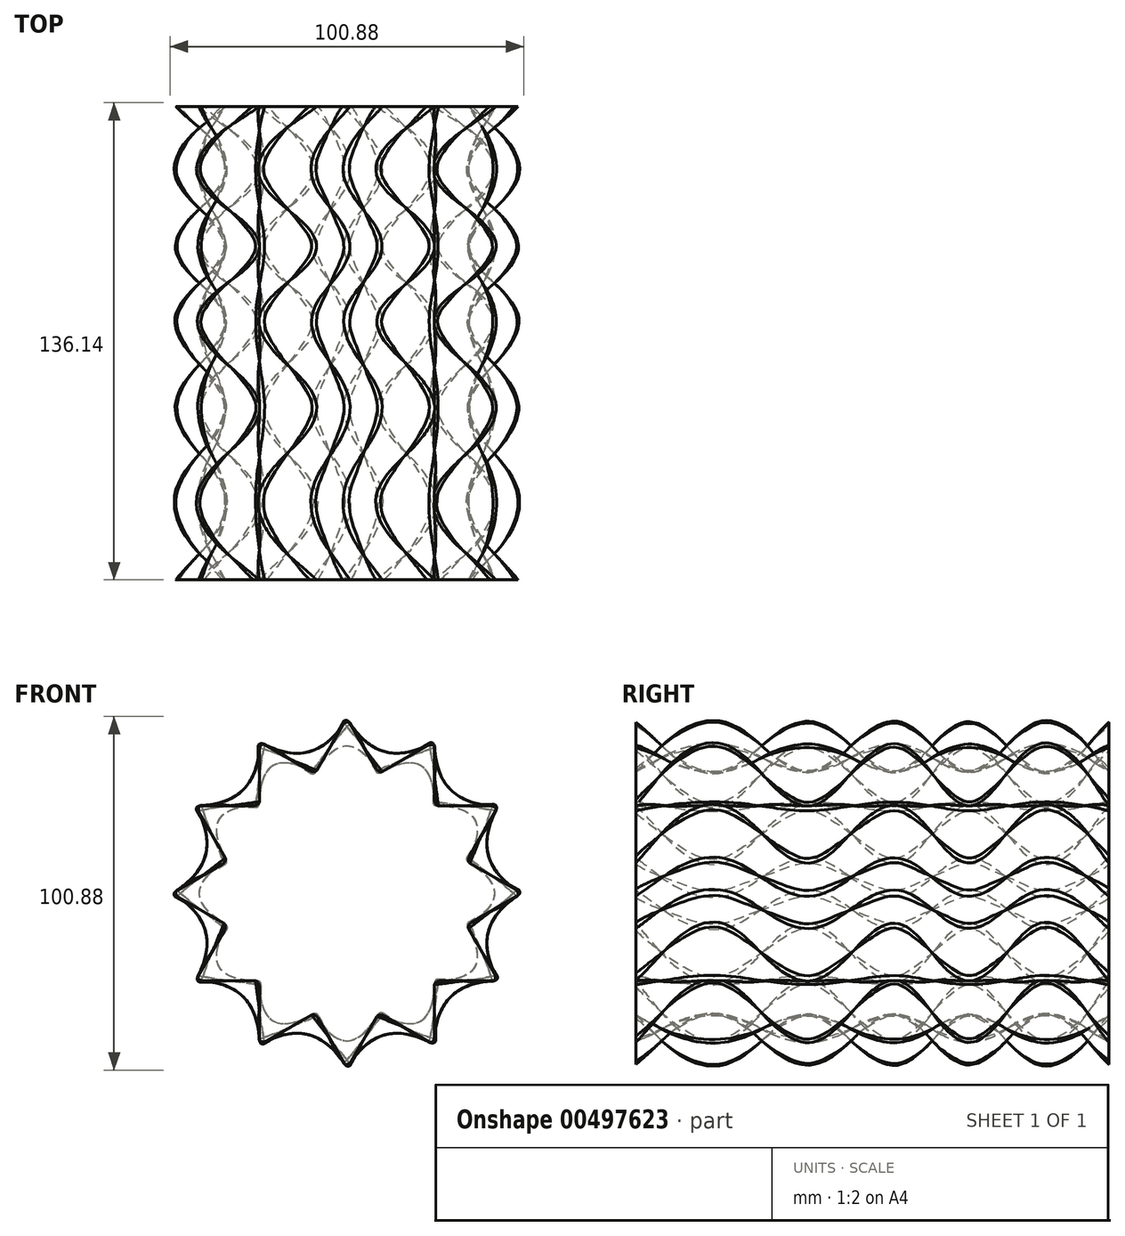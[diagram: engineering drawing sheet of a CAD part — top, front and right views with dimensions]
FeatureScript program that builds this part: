
annotation { "Feature Type Name" : "Feature", "Feature Type Description" : "" }
export const myFeature = defineFeature(function(context is Context, id is Id, definition is map)
    precondition{}
    {
        {
            var Q0;
            Q0=qCreatedBy(makeId("Front.planeOp"),FACE);
            cPlane(context, id + "F0", {"entities" : qUnion([Q0]), "cplaneType" : CPlaneType.OFFSET, "offset" : 20 * mm, "width" : 150 * mm, "height" : 150 * mm});
        }
        {
            var Q0;
            Q0=qCreatedBy(id+"F0.planeOp",FACE);
            cPlane(context, id + "F1", {"entities" : qUnion([Q0]), "cplaneType" : CPlaneType.OFFSET, "offset" : 20 * mm, "width" : 150 * mm, "height" : 150 * mm});
        }
        {
            var Q0;
            Q0=qCreatedBy(id+"F0.planeOp",FACE);
            cPlane(context, id + "F2", {"entities" : qUnion([Q0]), "cplaneType" : CPlaneType.OFFSET, "offset" : 40 * mm, "width" : 150 * mm, "height" : 150 * mm});
        }
        {
            var Q0;
            Q0=qCreatedBy(id+"F2.planeOp",FACE);
            cPlane(context, id + "F3", {"entities" : qUnion([Q0]), "cplaneType" : CPlaneType.OFFSET, "offset" : 25 * mm, "width" : 150 * mm, "height" : 150 * mm});
        }
        {
            var Q0;
            Q0=qCreatedBy(id+"F3.planeOp",FACE);
            cPlane(context, id + "F4", {"entities" : qUnion([Q0]), "cplaneType" : CPlaneType.OFFSET, "offset" : 25 * mm, "width" : 150 * mm, "height" : 150 * mm});
        }
        {
            var Q0;
            Q0=qCreatedBy(id+"F4.planeOp",FACE);
            cPlane(context, id + "F5", {"entities" : qUnion([Q0]), "cplaneType" : CPlaneType.OFFSET, "offset" : 25 * mm, "width" : 150 * mm, "height" : 150 * mm});
        }
        {
            var Q0;
            Q0=qCreatedBy(makeId("Front.planeOp"),FACE);
            var sketch = newSketch(context, id + "F6", { "sketchPlane" : qUnion([Q0])});
            skCircle(sketch, "E0", {"center": v(0, 0) * mm, "radius": 50 * mm});
            skCircle(sketch, "E1.cCircle", {"center": v(0, 0) * mm, "radius": 50 * mm, "construction": true});
            skLineSegment(sketch, "E1.0", {"start": v(50, 0) * mm, "end": v(34.15, -9.15) * mm});
            skLineSegment(sketch, "E1.1", {"start": v(-25, -43.3) * mm, "end": v(-25, -25) * mm});
            skLineSegment(sketch, "E1.2", {"start": v(-25, 43.3) * mm, "end": v(-9.15, 34.15) * mm});
            skPoint(sketch, "E2", {"position": v(12.5, 21.65) * mm});
            skLineSegment(sketch, "E3.0", {"start": v(0, 50) * mm, "end": v(9.15, 34.15) * mm});
            skLineSegment(sketch, "E3.1", {"start": v(43.3, -25) * mm, "end": v(25, -25) * mm});
            skLineSegment(sketch, "E3.2", {"start": v(-43.3, -25) * mm, "end": v(-34.15, -9.15) * mm});
            skLineSegment(sketch, "E4.0", {"start": v(25, 43.3) * mm, "end": v(25, 25) * mm});
            skLineSegment(sketch, "E4.1", {"start": v(25, -43.3) * mm, "end": v(9.15, -34.15) * mm});
            skLineSegment(sketch, "E4.2", {"start": v(-50, 0) * mm, "end": v(-34.15, 9.15) * mm});
            skLineSegment(sketch, "E5.0", {"start": v(43.3, 25) * mm, "end": v(34.15, 9.15) * mm});
            skLineSegment(sketch, "E5.1", {"start": v(0, -50) * mm, "end": v(-9.15, -34.15) * mm});
            skLineSegment(sketch, "E5.2", {"start": v(-43.3, 25) * mm, "end": v(-25, 25) * mm});
            skLineSegment(sketch, "E6.trimOffspring", {"start": v(34.15, 9.15) * mm, "end": v(50, 0) * mm});
            skLineSegment(sketch, "E7.trimOffspring", {"start": v(25, -25) * mm, "end": v(25, -43.3) * mm});
            skLineSegment(sketch, "E8.trimOffspring", {"start": v(25, 25) * mm, "end": v(43.3, 25) * mm});
            skLineSegment(sketch, "E9.trimOffspring", {"start": v(9.15, 34.15) * mm, "end": v(25, 43.3) * mm});
            skLineSegment(sketch, "E10.trimOffspring", {"start": v(-9.15, 34.15) * mm, "end": v(0, 50) * mm});
            skLineSegment(sketch, "E11.trimOffspring", {"start": v(-25, 25) * mm, "end": v(-25, 43.3) * mm});
            skLineSegment(sketch, "E12.trimOffspring", {"start": v(-34.15, 9.15) * mm, "end": v(-43.3, 25) * mm});
            skLineSegment(sketch, "E13.trimOffspring", {"start": v(-34.15, -9.15) * mm, "end": v(-50, 0) * mm});
            skLineSegment(sketch, "E14.trimOffspring", {"start": v(-25, -25) * mm, "end": v(-43.3, -25) * mm});
            skLineSegment(sketch, "E15.trimOffspring", {"start": v(-9.15, -34.15) * mm, "end": v(-25, -43.3) * mm});
            skLineSegment(sketch, "E16.trimOffspring", {"start": v(9.15, -34.15) * mm, "end": v(0, -50) * mm});
            skLineSegment(sketch, "E17.trimOffspring", {"start": v(34.15, -9.15) * mm, "end": v(43.3, -25) * mm});
            skSolve(sketch);
        }
        {
            var Q0;
            Q0=qCreatedBy(id+"F0.planeOp",FACE);
            var sketch = newSketch(context, id + "F7", { "sketchPlane" : qUnion([Q0])});
            skLineSegment(sketch, "E18", {"start": v(0, 50) * mm, "end": v(9.15, 34.15) * mm});
            skLineSegment(sketch, "E19", {"start": v(9.15, 34.15) * mm, "end": v(25, 43.3) * mm});
            skLineSegment(sketch, "E20.1.0", {"start": v(-25, 43.3) * mm, "end": v(-9.15, 34.15) * mm});
            skLineSegment(sketch, "E20.1.1", {"start": v(-9.15, 34.15) * mm, "end": v(0, 50) * mm});
            skLineSegment(sketch, "E20.2.0", {"start": v(-43.3, 25) * mm, "end": v(-25, 25) * mm});
            skLineSegment(sketch, "E20.2.1", {"start": v(-25, 25) * mm, "end": v(-25, 43.3) * mm});
            skLineSegment(sketch, "E20.3.0", {"start": v(-50, 0) * mm, "end": v(-34.15, 9.15) * mm});
            skLineSegment(sketch, "E20.3.1", {"start": v(-34.15, 9.15) * mm, "end": v(-43.3, 25) * mm});
            skLineSegment(sketch, "E20.4.0", {"start": v(-43.3, -25) * mm, "end": v(-34.15, -9.15) * mm});
            skLineSegment(sketch, "E20.4.1", {"start": v(-34.15, -9.15) * mm, "end": v(-50, 0) * mm});
            skLineSegment(sketch, "E20.5.0", {"start": v(-25, -43.3) * mm, "end": v(-25, -25) * mm});
            skLineSegment(sketch, "E20.5.1", {"start": v(-25, -25) * mm, "end": v(-43.3, -25) * mm});
            skLineSegment(sketch, "E20.6.0", {"start": v(0, -50) * mm, "end": v(-9.15, -34.15) * mm});
            skLineSegment(sketch, "E20.6.1", {"start": v(-9.15, -34.15) * mm, "end": v(-25, -43.3) * mm});
            skLineSegment(sketch, "E20.7.0", {"start": v(25, -43.3) * mm, "end": v(9.15, -34.15) * mm});
            skLineSegment(sketch, "E20.7.1", {"start": v(9.15, -34.15) * mm, "end": v(0, -50) * mm});
            skLineSegment(sketch, "E20.8.0", {"start": v(43.3, -25) * mm, "end": v(25, -25) * mm});
            skLineSegment(sketch, "E20.8.1", {"start": v(25, -25) * mm, "end": v(25, -43.3) * mm});
            skLineSegment(sketch, "E20.9.0", {"start": v(50, 0) * mm, "end": v(34.15, -9.15) * mm});
            skLineSegment(sketch, "E20.9.1", {"start": v(34.15, -9.15) * mm, "end": v(43.3, -25) * mm});
            skLineSegment(sketch, "E20.10.0", {"start": v(43.3, 25) * mm, "end": v(34.15, 9.15) * mm});
            skLineSegment(sketch, "E20.10.1", {"start": v(34.15, 9.15) * mm, "end": v(50, 0) * mm});
            skLineSegment(sketch, "E20.11.0", {"start": v(25, 43.3) * mm, "end": v(25, 25) * mm});
            skLineSegment(sketch, "E20.11.1", {"start": v(25, 25) * mm, "end": v(43.3, 25) * mm});
            skPoint(sketch, "E20.center", {"position": v(0, 0) * mm});
            skSolve(sketch);
        }
        {
            var Q0;
            Q0=qCreatedBy(id+"F2.planeOp",FACE);
            var sketch = newSketch(context, id + "F8", { "sketchPlane" : qUnion([Q0])});
            skPoint(sketch, "E21.center", {"position": v(0, 0) * mm});
            skLineSegment(sketch, "E22", {"start": v(-9.15, 34.15) * mm, "end": v(0, 50) * mm});
            skLineSegment(sketch, "E23", {"start": v(0, 50) * mm, "end": v(9.15, 34.15) * mm});
            skLineSegment(sketch, "E24.1.2", {"start": v(-25, 43.3) * mm, "end": v(-9.15, 34.15) * mm});
            skLineSegment(sketch, "E24.1.3", {"start": v(-25, 25) * mm, "end": v(-25, 43.3) * mm});
            skLineSegment(sketch, "E24.2.2", {"start": v(-43.3, 25) * mm, "end": v(-25, 25) * mm});
            skLineSegment(sketch, "E24.2.3", {"start": v(-34.15, 9.15) * mm, "end": v(-43.3, 25) * mm});
            skLineSegment(sketch, "E24.3.2", {"start": v(-50, 0) * mm, "end": v(-34.15, 9.15) * mm});
            skLineSegment(sketch, "E24.3.3", {"start": v(-34.15, -9.15) * mm, "end": v(-50, 0) * mm});
            skLineSegment(sketch, "E24.4.2", {"start": v(-43.3, -25) * mm, "end": v(-34.15, -9.15) * mm});
            skLineSegment(sketch, "E24.4.3", {"start": v(-25, -25) * mm, "end": v(-43.3, -25) * mm});
            skLineSegment(sketch, "E24.5.2", {"start": v(-25, -43.3) * mm, "end": v(-25, -25) * mm});
            skLineSegment(sketch, "E24.5.3", {"start": v(-9.15, -34.15) * mm, "end": v(-25, -43.3) * mm});
            skLineSegment(sketch, "E24.6.2", {"start": v(0, -50) * mm, "end": v(-9.15, -34.15) * mm});
            skLineSegment(sketch, "E24.6.3", {"start": v(9.15, -34.15) * mm, "end": v(0, -50) * mm});
            skLineSegment(sketch, "E24.7.2", {"start": v(25, -43.3) * mm, "end": v(9.15, -34.15) * mm});
            skLineSegment(sketch, "E24.7.3", {"start": v(25, -25) * mm, "end": v(25, -43.3) * mm});
            skLineSegment(sketch, "E24.8.2", {"start": v(43.3, -25) * mm, "end": v(25, -25) * mm});
            skLineSegment(sketch, "E24.8.3", {"start": v(34.15, -9.15) * mm, "end": v(43.3, -25) * mm});
            skLineSegment(sketch, "E24.9.2", {"start": v(50, 0) * mm, "end": v(34.15, -9.15) * mm});
            skLineSegment(sketch, "E24.9.3", {"start": v(34.15, 9.15) * mm, "end": v(50, 0) * mm});
            skLineSegment(sketch, "E24.10.2", {"start": v(43.3, 25) * mm, "end": v(34.15, 9.15) * mm});
            skLineSegment(sketch, "E24.10.3", {"start": v(25, 25) * mm, "end": v(43.3, 25) * mm});
            skLineSegment(sketch, "E24.11.2", {"start": v(25, 43.3) * mm, "end": v(25, 25) * mm});
            skLineSegment(sketch, "E24.11.3", {"start": v(9.15, 34.15) * mm, "end": v(25, 43.3) * mm});
            skSolve(sketch);
        }
        {
            var Q0;
            Q0=qCreatedBy(id+"F1.planeOp",FACE);
            var sketch = newSketch(context, id + "F9", { "sketchPlane" : qUnion([Q0])});
            skLineSegment(sketch, "E25", {"start": v(0, 50) * mm, "end": v(-9.15, 34.15) * mm});
            skLineSegment(sketch, "E26", {"start": v(0, 50) * mm, "end": v(9.15, 34.15) * mm});
            skLineSegment(sketch, "E27.1.0", {"start": v(-25, 43.3) * mm, "end": v(-9.15, 34.15) * mm});
            skLineSegment(sketch, "E27.1.1", {"start": v(-25, 43.3) * mm, "end": v(-25, 25) * mm});
            skLineSegment(sketch, "E27.2.0", {"start": v(-43.3, 25) * mm, "end": v(-25, 25) * mm});
            skLineSegment(sketch, "E27.2.1", {"start": v(-43.3, 25) * mm, "end": v(-34.15, 9.15) * mm});
            skLineSegment(sketch, "E27.3.0", {"start": v(-50, 0) * mm, "end": v(-34.15, 9.15) * mm});
            skLineSegment(sketch, "E27.3.1", {"start": v(-50, 0) * mm, "end": v(-34.15, -9.15) * mm});
            skLineSegment(sketch, "E27.4.0", {"start": v(-43.3, -25) * mm, "end": v(-34.15, -9.15) * mm});
            skLineSegment(sketch, "E27.4.1", {"start": v(-43.3, -25) * mm, "end": v(-25, -25) * mm});
            skLineSegment(sketch, "E27.5.0", {"start": v(-25, -43.3) * mm, "end": v(-25, -25) * mm});
            skLineSegment(sketch, "E27.5.1", {"start": v(-25, -43.3) * mm, "end": v(-9.15, -34.15) * mm});
            skLineSegment(sketch, "E27.6.0", {"start": v(0, -50) * mm, "end": v(-9.15, -34.15) * mm});
            skLineSegment(sketch, "E27.6.1", {"start": v(0, -50) * mm, "end": v(9.15, -34.15) * mm});
            skLineSegment(sketch, "E27.7.0", {"start": v(25, -43.3) * mm, "end": v(9.15, -34.15) * mm});
            skLineSegment(sketch, "E27.7.1", {"start": v(25, -43.3) * mm, "end": v(25, -25) * mm});
            skLineSegment(sketch, "E27.8.0", {"start": v(43.3, -25) * mm, "end": v(25, -25) * mm});
            skLineSegment(sketch, "E27.8.1", {"start": v(43.3, -25) * mm, "end": v(34.15, -9.15) * mm});
            skLineSegment(sketch, "E27.9.0", {"start": v(50, 0) * mm, "end": v(34.15, -9.15) * mm});
            skLineSegment(sketch, "E27.9.1", {"start": v(50, 0) * mm, "end": v(34.15, 9.15) * mm});
            skLineSegment(sketch, "E27.10.0", {"start": v(43.3, 25) * mm, "end": v(34.15, 9.15) * mm});
            skLineSegment(sketch, "E27.10.1", {"start": v(43.3, 25) * mm, "end": v(25, 25) * mm});
            skLineSegment(sketch, "E27.11.0", {"start": v(25, 43.3) * mm, "end": v(25, 25) * mm});
            skLineSegment(sketch, "E27.11.1", {"start": v(25, 43.3) * mm, "end": v(9.15, 34.15) * mm});
            skPoint(sketch, "E27.center", {"position": v(0, 0) * mm});
            skSolve(sketch);
        }
        {
            var Q0;
            Q0=qCreatedBy(id+"F3.planeOp",FACE);
            var sketch = newSketch(context, id + "F10", { "sketchPlane" : qUnion([Q0])});
            skCircle(sketch, "E28.cCircle", {"center": v(0, 0) * mm, "radius": 50 * mm, "construction": true});
            skLineSegment(sketch, "E29", {"start": v(0, 50) * mm, "end": v(9.15, 34.15) * mm});
            skLineSegment(sketch, "E30", {"start": v(25, 43.3) * mm, "end": v(9.15, 34.15) * mm});
            skLineSegment(sketch, "E31.1.0", {"start": v(0, 50) * mm, "end": v(-9.15, 34.15) * mm});
            skLineSegment(sketch, "E31.1.1", {"start": v(-25, 43.3) * mm, "end": v(-9.15, 34.15) * mm});
            skLineSegment(sketch, "E31.2.0", {"start": v(-25, 43.3) * mm, "end": v(-25, 25) * mm});
            skLineSegment(sketch, "E31.2.1", {"start": v(-43.3, 25) * mm, "end": v(-25, 25) * mm});
            skLineSegment(sketch, "E31.3.0", {"start": v(-43.3, 25) * mm, "end": v(-34.15, 9.15) * mm});
            skLineSegment(sketch, "E31.3.1", {"start": v(-50, 0) * mm, "end": v(-34.15, 9.15) * mm});
            skLineSegment(sketch, "E31.4.0", {"start": v(-50, 0) * mm, "end": v(-34.15, -9.15) * mm});
            skLineSegment(sketch, "E31.4.1", {"start": v(-43.3, -25) * mm, "end": v(-34.15, -9.15) * mm});
            skLineSegment(sketch, "E31.5.0", {"start": v(-43.3, -25) * mm, "end": v(-25, -25) * mm});
            skLineSegment(sketch, "E31.5.1", {"start": v(-25, -43.3) * mm, "end": v(-25, -25) * mm});
            skLineSegment(sketch, "E31.6.0", {"start": v(-25, -43.3) * mm, "end": v(-9.15, -34.15) * mm});
            skLineSegment(sketch, "E31.6.1", {"start": v(0, -50) * mm, "end": v(-9.15, -34.15) * mm});
            skLineSegment(sketch, "E31.7.0", {"start": v(0, -50) * mm, "end": v(9.15, -34.15) * mm});
            skLineSegment(sketch, "E31.7.1", {"start": v(25, -43.3) * mm, "end": v(9.15, -34.15) * mm});
            skLineSegment(sketch, "E31.8.0", {"start": v(25, -43.3) * mm, "end": v(25, -25) * mm});
            skLineSegment(sketch, "E31.8.1", {"start": v(43.3, -25) * mm, "end": v(25, -25) * mm});
            skLineSegment(sketch, "E31.9.0", {"start": v(43.3, -25) * mm, "end": v(34.15, -9.15) * mm});
            skLineSegment(sketch, "E31.9.1", {"start": v(50, 0) * mm, "end": v(34.15, -9.15) * mm});
            skLineSegment(sketch, "E31.10.0", {"start": v(50, 0) * mm, "end": v(34.15, 9.15) * mm});
            skLineSegment(sketch, "E31.10.1", {"start": v(43.3, 25) * mm, "end": v(34.15, 9.15) * mm});
            skLineSegment(sketch, "E31.11.0", {"start": v(43.3, 25) * mm, "end": v(25, 25) * mm});
            skLineSegment(sketch, "E31.11.1", {"start": v(25, 43.3) * mm, "end": v(25, 25) * mm});
            skSolve(sketch);
        }
        {
            var Q0;
            Q0=qCreatedBy(id+"F4.planeOp",FACE);
            var sketch = newSketch(context, id + "F11", { "sketchPlane" : qUnion([Q0])});
            skLineSegment(sketch, "E32", {"start": v(0, 50) * mm, "end": v(9.15, 34.15) * mm});
            skLineSegment(sketch, "E33", {"start": v(25, 43.3) * mm, "end": v(9.15, 34.15) * mm});
            skLineSegment(sketch, "E34.1.0", {"start": v(0, 50) * mm, "end": v(-9.15, 34.15) * mm});
            skLineSegment(sketch, "E34.1.1", {"start": v(-25, 43.3) * mm, "end": v(-9.15, 34.15) * mm});
            skLineSegment(sketch, "E34.2.0", {"start": v(-25, 43.3) * mm, "end": v(-25, 25) * mm});
            skLineSegment(sketch, "E34.2.1", {"start": v(-43.3, 25) * mm, "end": v(-25, 25) * mm});
            skLineSegment(sketch, "E34.3.0", {"start": v(-43.3, 25) * mm, "end": v(-34.15, 9.15) * mm});
            skLineSegment(sketch, "E34.3.1", {"start": v(-50, 0) * mm, "end": v(-34.15, 9.15) * mm});
            skLineSegment(sketch, "E34.4.0", {"start": v(-50, 0) * mm, "end": v(-34.15, -9.15) * mm});
            skLineSegment(sketch, "E34.4.1", {"start": v(-43.3, -25) * mm, "end": v(-34.15, -9.15) * mm});
            skLineSegment(sketch, "E34.5.0", {"start": v(-43.3, -25) * mm, "end": v(-25, -25) * mm});
            skLineSegment(sketch, "E34.5.1", {"start": v(-25, -43.3) * mm, "end": v(-25, -25) * mm});
            skLineSegment(sketch, "E34.6.0", {"start": v(-25, -43.3) * mm, "end": v(-9.15, -34.15) * mm});
            skLineSegment(sketch, "E34.6.1", {"start": v(0, -50) * mm, "end": v(-9.15, -34.15) * mm});
            skLineSegment(sketch, "E34.7.0", {"start": v(0, -50) * mm, "end": v(9.15, -34.15) * mm});
            skLineSegment(sketch, "E34.7.1", {"start": v(25, -43.3) * mm, "end": v(9.15, -34.15) * mm});
            skLineSegment(sketch, "E34.8.0", {"start": v(25, -43.3) * mm, "end": v(25, -25) * mm});
            skLineSegment(sketch, "E34.8.1", {"start": v(43.3, -25) * mm, "end": v(25, -25) * mm});
            skLineSegment(sketch, "E34.9.0", {"start": v(43.3, -25) * mm, "end": v(34.15, -9.15) * mm});
            skLineSegment(sketch, "E34.9.1", {"start": v(50, 0) * mm, "end": v(34.15, -9.15) * mm});
            skLineSegment(sketch, "E34.10.0", {"start": v(50, 0) * mm, "end": v(34.15, 9.15) * mm});
            skLineSegment(sketch, "E34.10.1", {"start": v(43.3, 25) * mm, "end": v(34.15, 9.15) * mm});
            skLineSegment(sketch, "E34.11.0", {"start": v(43.3, 25) * mm, "end": v(25, 25) * mm});
            skLineSegment(sketch, "E34.11.1", {"start": v(25, 43.3) * mm, "end": v(25, 25) * mm});
            skPoint(sketch, "E34.center", {"position": v(0, 0) * mm});
            skSolve(sketch);
        }
        {
            var Q0;
            Q0=qCreatedBy(id+"F5.planeOp",FACE);
            var sketch = newSketch(context, id + "F12", { "sketchPlane" : qUnion([Q0])});
            skLineSegment(sketch, "E35", {"start": v(0, 50) * mm, "end": v(9.15, 34.15) * mm});
            skLineSegment(sketch, "E36", {"start": v(9.15, 34.15) * mm, "end": v(25, 43.3) * mm});
            skLineSegment(sketch, "E37.1.0", {"start": v(-9.15, 34.15) * mm, "end": v(0, 50) * mm});
            skLineSegment(sketch, "E37.1.1", {"start": v(-25, 43.3) * mm, "end": v(-9.15, 34.15) * mm});
            skLineSegment(sketch, "E37.2.0", {"start": v(-25, 25) * mm, "end": v(-25, 43.3) * mm});
            skLineSegment(sketch, "E37.2.1", {"start": v(-43.3, 25) * mm, "end": v(-25, 25) * mm});
            skLineSegment(sketch, "E37.3.0", {"start": v(-34.15, 9.15) * mm, "end": v(-43.3, 25) * mm});
            skLineSegment(sketch, "E37.3.1", {"start": v(-50, 0) * mm, "end": v(-34.15, 9.15) * mm});
            skLineSegment(sketch, "E37.4.0", {"start": v(-34.15, -9.15) * mm, "end": v(-50, 0) * mm});
            skLineSegment(sketch, "E37.4.1", {"start": v(-43.3, -25) * mm, "end": v(-34.15, -9.15) * mm});
            skLineSegment(sketch, "E37.5.0", {"start": v(-25, -25) * mm, "end": v(-43.3, -25) * mm});
            skLineSegment(sketch, "E37.5.1", {"start": v(-25, -43.3) * mm, "end": v(-25, -25) * mm});
            skLineSegment(sketch, "E37.6.0", {"start": v(-9.15, -34.15) * mm, "end": v(-25, -43.3) * mm});
            skLineSegment(sketch, "E37.6.1", {"start": v(0, -50) * mm, "end": v(-9.15, -34.15) * mm});
            skLineSegment(sketch, "E37.7.0", {"start": v(9.15, -34.15) * mm, "end": v(0, -50) * mm});
            skLineSegment(sketch, "E37.7.1", {"start": v(25, -43.3) * mm, "end": v(9.15, -34.15) * mm});
            skLineSegment(sketch, "E37.8.0", {"start": v(25, -25) * mm, "end": v(25, -43.3) * mm});
            skLineSegment(sketch, "E37.8.1", {"start": v(43.3, -25) * mm, "end": v(25, -25) * mm});
            skLineSegment(sketch, "E37.9.0", {"start": v(34.15, -9.15) * mm, "end": v(43.3, -25) * mm});
            skLineSegment(sketch, "E37.9.1", {"start": v(50, 0) * mm, "end": v(34.15, -9.15) * mm});
            skLineSegment(sketch, "E37.10.0", {"start": v(34.15, 9.15) * mm, "end": v(50, 0) * mm});
            skLineSegment(sketch, "E37.10.1", {"start": v(43.3, 25) * mm, "end": v(34.15, 9.15) * mm});
            skLineSegment(sketch, "E37.11.0", {"start": v(25, 25) * mm, "end": v(43.3, 25) * mm});
            skLineSegment(sketch, "E37.11.1", {"start": v(25, 43.3) * mm, "end": v(25, 25) * mm});
            skPoint(sketch, "E37.center", {"position": v(0, 0) * mm});
            skSolve(sketch);
        }
        {
            var Q0;
            Q0=makeQuery(id+"F6.imprint","IMPRINT",FACE,{"disambiguationData":[TD([[makeQuery(id+"F6.imprint","IMPRINT",EDGE,{"derivedFrom":sQuery(id+"F6.wireOp",EDGE,"E1.0")}),-1.0]])]});
            var Q1;
            Q1=makeQuery(id+"F7.imprint","IMPRINT",FACE,{"disambiguationData":[TD([[makeQuery(id+"F7.imprint","IMPRINT",EDGE,{"derivedFrom":sQuery(id+"F7.wireOp",EDGE,"E18")}),-1.0]])]});
            var Q2;
            Q2=makeQuery(id+"F9.imprint","IMPRINT",FACE,{"disambiguationData":[TD([[makeQuery(id+"F9.imprint","IMPRINT",EDGE,{"derivedFrom":sQuery(id+"F9.wireOp",EDGE,"E25")}),1.0]])]});
            var Q3;
            Q3=makeQuery(id+"F8.imprint","IMPRINT",FACE,{"disambiguationData":[TD([[makeQuery(id+"F8.imprint","IMPRINT",EDGE,{"derivedFrom":sQuery(id+"F8.wireOp",EDGE,"E22")}),-1.0]])]});
            var Q4;
            Q4=makeQuery(id+"F10.imprint","IMPRINT",FACE,{"disambiguationData":[TD([[makeQuery(id+"F10.imprint","IMPRINT",EDGE,{"derivedFrom":sQuery(id+"F10.wireOp",EDGE,"E29")}),-1.0]])]});
            var Q5;
            Q5=makeQuery(id+"F11.imprint","IMPRINT",FACE,{"disambiguationData":[TD([[makeQuery(id+"F11.imprint","IMPRINT",EDGE,{"derivedFrom":sQuery(id+"F11.wireOp",EDGE,"E32")}),-1.0]])]});
            var Q6;
            Q6=makeQuery(id+"F12.imprint","IMPRINT",FACE,{"disambiguationData":[TD([[makeQuery(id+"F12.imprint","IMPRINT",EDGE,{"derivedFrom":sQuery(id+"F12.wireOp",EDGE,"E35")}),-1.0]])]});
            var Q7;
            Q7=sQuery(id+"F6.wireOp",VERTEX,"E4.0.start");
            var Q8;
            Q8=sQuery(id+"F7.wireOp",VERTEX,"E19.start");
            var Q9;
            Q9=sQuery(id+"F9.wireOp",VERTEX,"E27.11.0.start");
            var Q10;
            Q10=sQuery(id+"F8.wireOp",VERTEX,"E23.end");
            var Q11;
            Q11=sQuery(id+"F10.wireOp",VERTEX,"E31.11.1.start");
            var Q12;
            Q12=sQuery(id+"F11.wireOp",VERTEX,"E33.end");
            var Q13;
            Q13=sQuery(id+"F12.wireOp",VERTEX,"E37.11.1.start");
            loft(context, id + "F13", {"sheetProfilesArray" : [{ "sheetProfileEntities" : qUnion([Q0]) }, { "sheetProfileEntities" : qUnion([Q1]) }, { "sheetProfileEntities" : qUnion([Q2]) }, { "sheetProfileEntities" : qUnion([Q3]) }, { "sheetProfileEntities" : qUnion([Q4]) }, { "sheetProfileEntities" : qUnion([Q5]) }, { "sheetProfileEntities" : qUnion([Q6]) }], "matchConnections" : true, "connections" : [{ "connectionEntities" : qUnion([Q7, Q8, Q9, Q10, Q11, Q12, Q13]), "connectionEdgeQueries" : qUnion([]), "connectionEdgeParameters" : [] }]});
        }
        {
            var Q0;
            {var subQ0=sQuery(id+"F6.wireOp",EDGE,"E0");Q0=qUnion([makeQuery(id+"F13.opLoft","SWEPT_EDGE",EDGE,{"disambiguationData":[OSD([subQ0,sQuery(id+"F6.wireOp",EDGE,"E4.1"),sQuery(id+"F6.wireOp",EDGE,"E7.trimOffspring"),sQuery(id+"F7.wireOp",EDGE,"E20.8.0"),sQuery(id+"F7.wireOp",EDGE,"E20.8.1"),sQuery(id+"F8.wireOp",EDGE,"E24.7.3"),sQuery(id+"F8.wireOp",EDGE,"E24.8.2"),sQuery(id+"F9.wireOp",EDGE,"E27.7.0"),sQuery(id+"F9.wireOp",EDGE,"E27.7.1"),sQuery(id+"F10.wireOp",EDGE,"E31.7.1"),sQuery(id+"F10.wireOp",EDGE,"E31.8.0"),sQuery(id+"F11.wireOp",EDGE,"E34.8.0"),sQuery(id+"F11.wireOp",EDGE,"E34.8.1"),sQuery(id+"F12.wireOp",EDGE,"E37.7.1"),sQuery(id+"F12.wireOp",EDGE,"E37.8.0")])]}),makeQuery(id+"F13.opLoft","SWEPT_EDGE",EDGE,{"disambiguationData":[OSD([subQ0,sQuery(id+"F6.wireOp",EDGE,"E5.1"),sQuery(id+"F6.wireOp",EDGE,"E16.trimOffspring"),sQuery(id+"F7.wireOp",EDGE,"E20.7.0"),sQuery(id+"F7.wireOp",EDGE,"E20.7.1"),sQuery(id+"F8.wireOp",EDGE,"E24.6.3"),sQuery(id+"F8.wireOp",EDGE,"E24.7.2"),sQuery(id+"F9.wireOp",EDGE,"E27.6.0"),sQuery(id+"F9.wireOp",EDGE,"E27.6.1"),sQuery(id+"F10.wireOp",EDGE,"E31.6.1"),sQuery(id+"F10.wireOp",EDGE,"E31.7.0"),sQuery(id+"F11.wireOp",EDGE,"E34.7.0"),sQuery(id+"F11.wireOp",EDGE,"E34.7.1"),sQuery(id+"F12.wireOp",EDGE,"E37.6.1"),sQuery(id+"F12.wireOp",EDGE,"E37.7.0")])]})]);}
            var Q1;
            {Q1=qUnion([makeQuery(id+"F13.opLoft","SWEPT_EDGE",EDGE,{"disambiguationData":[OSD([sQuery(id+"F6.wireOp",EDGE,"E3.1"),sQuery(id+"F6.wireOp",EDGE,"E7.trimOffspring"),sQuery(id+"F7.wireOp",EDGE,"E20.8.0"),sQuery(id+"F7.wireOp",EDGE,"E20.9.1"),sQuery(id+"F8.wireOp",EDGE,"E24.8.2"),sQuery(id+"F8.wireOp",EDGE,"E24.8.3"),sQuery(id+"F9.wireOp",EDGE,"E27.7.1"),sQuery(id+"F9.wireOp",EDGE,"E27.8.0"),sQuery(id+"F10.wireOp",EDGE,"E31.8.0"),sQuery(id+"F10.wireOp",EDGE,"E31.8.1"),sQuery(id+"F11.wireOp",EDGE,"E34.8.1"),sQuery(id+"F11.wireOp",EDGE,"E34.9.0"),sQuery(id+"F12.wireOp",EDGE,"E37.8.0"),sQuery(id+"F12.wireOp",EDGE,"E37.8.1")])]}),makeQuery(id+"F13.opLoft","SWEPT_EDGE",EDGE,{"disambiguationData":[OSD([sQuery(id+"F6.wireOp",EDGE,"E4.1"),sQuery(id+"F6.wireOp",EDGE,"E16.trimOffspring"),sQuery(id+"F7.wireOp",EDGE,"E20.7.0"),sQuery(id+"F7.wireOp",EDGE,"E20.8.1"),sQuery(id+"F8.wireOp",EDGE,"E24.7.2"),sQuery(id+"F8.wireOp",EDGE,"E24.7.3"),sQuery(id+"F9.wireOp",EDGE,"E27.6.1"),sQuery(id+"F9.wireOp",EDGE,"E27.7.0"),sQuery(id+"F10.wireOp",EDGE,"E31.7.0"),sQuery(id+"F10.wireOp",EDGE,"E31.7.1"),sQuery(id+"F11.wireOp",EDGE,"E34.7.1"),sQuery(id+"F11.wireOp",EDGE,"E34.8.0"),sQuery(id+"F12.wireOp",EDGE,"E37.7.0"),sQuery(id+"F12.wireOp",EDGE,"E37.7.1")])]})]);}
            var Q2;
            {Q2=qUnion([makeQuery(id+"F13.opLoft","SWEPT_EDGE",EDGE,{"disambiguationData":[OSD([sQuery(id+"F6.wireOp",EDGE,"E4.1"),sQuery(id+"F6.wireOp",EDGE,"E16.trimOffspring"),sQuery(id+"F7.wireOp",EDGE,"E20.7.0"),sQuery(id+"F7.wireOp",EDGE,"E20.8.1"),sQuery(id+"F8.wireOp",EDGE,"E24.7.2"),sQuery(id+"F8.wireOp",EDGE,"E24.7.3"),sQuery(id+"F9.wireOp",EDGE,"E27.6.1"),sQuery(id+"F9.wireOp",EDGE,"E27.7.0"),sQuery(id+"F10.wireOp",EDGE,"E31.7.0"),sQuery(id+"F10.wireOp",EDGE,"E31.7.1"),sQuery(id+"F11.wireOp",EDGE,"E34.7.1"),sQuery(id+"F11.wireOp",EDGE,"E34.8.0"),sQuery(id+"F12.wireOp",EDGE,"E37.7.0"),sQuery(id+"F12.wireOp",EDGE,"E37.7.1")])]}),makeQuery(id+"F13.opLoft","SWEPT_EDGE",EDGE,{"disambiguationData":[OSD([sQuery(id+"F6.wireOp",EDGE,"E5.1"),sQuery(id+"F6.wireOp",EDGE,"E15.trimOffspring"),sQuery(id+"F7.wireOp",EDGE,"E20.6.0"),sQuery(id+"F7.wireOp",EDGE,"E20.7.1"),sQuery(id+"F8.wireOp",EDGE,"E24.6.2"),sQuery(id+"F8.wireOp",EDGE,"E24.6.3"),sQuery(id+"F9.wireOp",EDGE,"E27.5.1"),sQuery(id+"F9.wireOp",EDGE,"E27.6.0"),sQuery(id+"F10.wireOp",EDGE,"E31.6.0"),sQuery(id+"F10.wireOp",EDGE,"E31.6.1"),sQuery(id+"F11.wireOp",EDGE,"E34.6.1"),sQuery(id+"F11.wireOp",EDGE,"E34.7.0"),sQuery(id+"F12.wireOp",EDGE,"E37.6.0"),sQuery(id+"F12.wireOp",EDGE,"E37.6.1")])]})]);}
            var Q3;
            {var subQ0=sQuery(id+"F6.wireOp",EDGE,"E0");Q3=qUnion([makeQuery(id+"F13.opLoft","SWEPT_EDGE",EDGE,{"disambiguationData":[OSD([subQ0,sQuery(id+"F6.wireOp",EDGE,"E1.1"),sQuery(id+"F6.wireOp",EDGE,"E15.trimOffspring"),sQuery(id+"F7.wireOp",EDGE,"E20.6.0"),sQuery(id+"F7.wireOp",EDGE,"E20.6.1"),sQuery(id+"F8.wireOp",EDGE,"E24.5.3"),sQuery(id+"F8.wireOp",EDGE,"E24.6.2"),sQuery(id+"F9.wireOp",EDGE,"E27.5.0"),sQuery(id+"F9.wireOp",EDGE,"E27.5.1"),sQuery(id+"F10.wireOp",EDGE,"E31.5.1"),sQuery(id+"F10.wireOp",EDGE,"E31.6.0"),sQuery(id+"F11.wireOp",EDGE,"E34.6.0"),sQuery(id+"F11.wireOp",EDGE,"E34.6.1"),sQuery(id+"F12.wireOp",EDGE,"E37.5.1"),sQuery(id+"F12.wireOp",EDGE,"E37.6.0")])]}),makeQuery(id+"F13.opLoft","SWEPT_EDGE",EDGE,{"disambiguationData":[OSD([subQ0,sQuery(id+"F6.wireOp",EDGE,"E5.1"),sQuery(id+"F6.wireOp",EDGE,"E16.trimOffspring"),sQuery(id+"F7.wireOp",EDGE,"E20.7.0"),sQuery(id+"F7.wireOp",EDGE,"E20.7.1"),sQuery(id+"F8.wireOp",EDGE,"E24.6.3"),sQuery(id+"F8.wireOp",EDGE,"E24.7.2"),sQuery(id+"F9.wireOp",EDGE,"E27.6.0"),sQuery(id+"F9.wireOp",EDGE,"E27.6.1"),sQuery(id+"F10.wireOp",EDGE,"E31.6.1"),sQuery(id+"F10.wireOp",EDGE,"E31.7.0"),sQuery(id+"F11.wireOp",EDGE,"E34.7.0"),sQuery(id+"F11.wireOp",EDGE,"E34.7.1"),sQuery(id+"F12.wireOp",EDGE,"E37.6.1"),sQuery(id+"F12.wireOp",EDGE,"E37.7.0")])]})]);}
            var Q4;
            {Q4=qUnion([makeQuery(id+"F13.opLoft","SWEPT_EDGE",EDGE,{"disambiguationData":[OSD([sQuery(id+"F6.wireOp",EDGE,"E1.1"),sQuery(id+"F6.wireOp",EDGE,"E14.trimOffspring"),sQuery(id+"F7.wireOp",EDGE,"E20.5.0"),sQuery(id+"F7.wireOp",EDGE,"E20.6.1"),sQuery(id+"F8.wireOp",EDGE,"E24.5.2"),sQuery(id+"F8.wireOp",EDGE,"E24.5.3"),sQuery(id+"F9.wireOp",EDGE,"E27.4.1"),sQuery(id+"F9.wireOp",EDGE,"E27.5.0"),sQuery(id+"F10.wireOp",EDGE,"E31.5.0"),sQuery(id+"F10.wireOp",EDGE,"E31.5.1"),sQuery(id+"F11.wireOp",EDGE,"E34.5.1"),sQuery(id+"F11.wireOp",EDGE,"E34.6.0"),sQuery(id+"F12.wireOp",EDGE,"E37.5.0"),sQuery(id+"F12.wireOp",EDGE,"E37.5.1")])]}),makeQuery(id+"F13.opLoft","SWEPT_EDGE",EDGE,{"disambiguationData":[OSD([sQuery(id+"F6.wireOp",EDGE,"E5.1"),sQuery(id+"F6.wireOp",EDGE,"E15.trimOffspring"),sQuery(id+"F7.wireOp",EDGE,"E20.6.0"),sQuery(id+"F7.wireOp",EDGE,"E20.7.1"),sQuery(id+"F8.wireOp",EDGE,"E24.6.2"),sQuery(id+"F8.wireOp",EDGE,"E24.6.3"),sQuery(id+"F9.wireOp",EDGE,"E27.5.1"),sQuery(id+"F9.wireOp",EDGE,"E27.6.0"),sQuery(id+"F10.wireOp",EDGE,"E31.6.0"),sQuery(id+"F10.wireOp",EDGE,"E31.6.1"),sQuery(id+"F11.wireOp",EDGE,"E34.6.1"),sQuery(id+"F11.wireOp",EDGE,"E34.7.0"),sQuery(id+"F12.wireOp",EDGE,"E37.6.0"),sQuery(id+"F12.wireOp",EDGE,"E37.6.1")])]})]);}
            var Q5;
            {var subQ0=sQuery(id+"F6.wireOp",EDGE,"E0");Q5=qUnion([makeQuery(id+"F13.opLoft","SWEPT_EDGE",EDGE,{"disambiguationData":[OSD([subQ0,sQuery(id+"F6.wireOp",EDGE,"E3.1"),sQuery(id+"F6.wireOp",EDGE,"E17.trimOffspring"),sQuery(id+"F7.wireOp",EDGE,"E20.9.0"),sQuery(id+"F7.wireOp",EDGE,"E20.9.1"),sQuery(id+"F8.wireOp",EDGE,"E24.8.3"),sQuery(id+"F8.wireOp",EDGE,"E24.9.2"),sQuery(id+"F9.wireOp",EDGE,"E27.8.0"),sQuery(id+"F9.wireOp",EDGE,"E27.8.1"),sQuery(id+"F10.wireOp",EDGE,"E31.8.1"),sQuery(id+"F10.wireOp",EDGE,"E31.9.0"),sQuery(id+"F11.wireOp",EDGE,"E34.9.0"),sQuery(id+"F11.wireOp",EDGE,"E34.9.1"),sQuery(id+"F12.wireOp",EDGE,"E37.8.1"),sQuery(id+"F12.wireOp",EDGE,"E37.9.0")])]}),makeQuery(id+"F13.opLoft","SWEPT_EDGE",EDGE,{"disambiguationData":[OSD([subQ0,sQuery(id+"F6.wireOp",EDGE,"E4.1"),sQuery(id+"F6.wireOp",EDGE,"E7.trimOffspring"),sQuery(id+"F7.wireOp",EDGE,"E20.8.0"),sQuery(id+"F7.wireOp",EDGE,"E20.8.1"),sQuery(id+"F8.wireOp",EDGE,"E24.7.3"),sQuery(id+"F8.wireOp",EDGE,"E24.8.2"),sQuery(id+"F9.wireOp",EDGE,"E27.7.0"),sQuery(id+"F9.wireOp",EDGE,"E27.7.1"),sQuery(id+"F10.wireOp",EDGE,"E31.7.1"),sQuery(id+"F10.wireOp",EDGE,"E31.8.0"),sQuery(id+"F11.wireOp",EDGE,"E34.8.0"),sQuery(id+"F11.wireOp",EDGE,"E34.8.1"),sQuery(id+"F12.wireOp",EDGE,"E37.7.1"),sQuery(id+"F12.wireOp",EDGE,"E37.8.0")])]})]);}
            var Q6;
            {var subQ0=sQuery(id+"F6.wireOp",EDGE,"E0");Q6=qUnion([makeQuery(id+"F13.opLoft","SWEPT_EDGE",EDGE,{"disambiguationData":[OSD([subQ0,sQuery(id+"F6.wireOp",EDGE,"E3.1"),sQuery(id+"F6.wireOp",EDGE,"E17.trimOffspring"),sQuery(id+"F7.wireOp",EDGE,"E20.9.0"),sQuery(id+"F7.wireOp",EDGE,"E20.9.1"),sQuery(id+"F8.wireOp",EDGE,"E24.8.3"),sQuery(id+"F8.wireOp",EDGE,"E24.9.2"),sQuery(id+"F9.wireOp",EDGE,"E27.8.0"),sQuery(id+"F9.wireOp",EDGE,"E27.8.1"),sQuery(id+"F10.wireOp",EDGE,"E31.8.1"),sQuery(id+"F10.wireOp",EDGE,"E31.9.0"),sQuery(id+"F11.wireOp",EDGE,"E34.9.0"),sQuery(id+"F11.wireOp",EDGE,"E34.9.1"),sQuery(id+"F12.wireOp",EDGE,"E37.8.1"),sQuery(id+"F12.wireOp",EDGE,"E37.9.0")])]}),makeQuery(id+"F13.opLoft","SWEPT_EDGE",EDGE,{"disambiguationData":[OSD([subQ0,sQuery(id+"F6.wireOp",EDGE,"E4.1"),sQuery(id+"F6.wireOp",EDGE,"E7.trimOffspring"),sQuery(id+"F7.wireOp",EDGE,"E20.8.0"),sQuery(id+"F7.wireOp",EDGE,"E20.8.1"),sQuery(id+"F8.wireOp",EDGE,"E24.7.3"),sQuery(id+"F8.wireOp",EDGE,"E24.8.2"),sQuery(id+"F9.wireOp",EDGE,"E27.7.0"),sQuery(id+"F9.wireOp",EDGE,"E27.7.1"),sQuery(id+"F10.wireOp",EDGE,"E31.7.1"),sQuery(id+"F10.wireOp",EDGE,"E31.8.0"),sQuery(id+"F11.wireOp",EDGE,"E34.8.0"),sQuery(id+"F11.wireOp",EDGE,"E34.8.1"),sQuery(id+"F12.wireOp",EDGE,"E37.7.1"),sQuery(id+"F12.wireOp",EDGE,"E37.8.0")])]})]);}
            var Q7;
            {Q7=qUnion([makeQuery(id+"F13.opLoft","SWEPT_EDGE",EDGE,{"disambiguationData":[OSD([sQuery(id+"F6.wireOp",EDGE,"E1.0"),sQuery(id+"F6.wireOp",EDGE,"E17.trimOffspring"),sQuery(id+"F7.wireOp",EDGE,"E20.9.0"),sQuery(id+"F7.wireOp",EDGE,"E20.10.1"),sQuery(id+"F8.wireOp",EDGE,"E24.9.2"),sQuery(id+"F8.wireOp",EDGE,"E24.9.3"),sQuery(id+"F9.wireOp",EDGE,"E27.8.1"),sQuery(id+"F9.wireOp",EDGE,"E27.9.0"),sQuery(id+"F10.wireOp",EDGE,"E31.9.0"),sQuery(id+"F10.wireOp",EDGE,"E31.9.1"),sQuery(id+"F11.wireOp",EDGE,"E34.9.1"),sQuery(id+"F11.wireOp",EDGE,"E34.10.0"),sQuery(id+"F12.wireOp",EDGE,"E37.9.0"),sQuery(id+"F12.wireOp",EDGE,"E37.9.1")])]}),makeQuery(id+"F13.opLoft","SWEPT_EDGE",EDGE,{"disambiguationData":[OSD([sQuery(id+"F6.wireOp",EDGE,"E3.1"),sQuery(id+"F6.wireOp",EDGE,"E7.trimOffspring"),sQuery(id+"F7.wireOp",EDGE,"E20.8.0"),sQuery(id+"F7.wireOp",EDGE,"E20.9.1"),sQuery(id+"F8.wireOp",EDGE,"E24.8.2"),sQuery(id+"F8.wireOp",EDGE,"E24.8.3"),sQuery(id+"F9.wireOp",EDGE,"E27.7.1"),sQuery(id+"F9.wireOp",EDGE,"E27.8.0"),sQuery(id+"F10.wireOp",EDGE,"E31.8.0"),sQuery(id+"F10.wireOp",EDGE,"E31.8.1"),sQuery(id+"F11.wireOp",EDGE,"E34.8.1"),sQuery(id+"F11.wireOp",EDGE,"E34.9.0"),sQuery(id+"F12.wireOp",EDGE,"E37.8.0"),sQuery(id+"F12.wireOp",EDGE,"E37.8.1")])]})]);}
            var Q8;
            {var subQ0=sQuery(id+"F6.wireOp",EDGE,"E0");Q8=qUnion([makeQuery(id+"F13.opLoft","SWEPT_EDGE",EDGE,{"disambiguationData":[OSD([subQ0,sQuery(id+"F6.wireOp",EDGE,"E1.0"),sQuery(id+"F6.wireOp",EDGE,"E6.trimOffspring"),sQuery(id+"F7.wireOp",EDGE,"E20.10.0"),sQuery(id+"F7.wireOp",EDGE,"E20.10.1"),sQuery(id+"F8.wireOp",EDGE,"E24.9.3"),sQuery(id+"F8.wireOp",EDGE,"E24.10.2"),sQuery(id+"F9.wireOp",EDGE,"E27.9.0"),sQuery(id+"F9.wireOp",EDGE,"E27.9.1"),sQuery(id+"F10.wireOp",EDGE,"E31.9.1"),sQuery(id+"F10.wireOp",EDGE,"E31.10.0"),sQuery(id+"F11.wireOp",EDGE,"E34.10.0"),sQuery(id+"F11.wireOp",EDGE,"E34.10.1"),sQuery(id+"F12.wireOp",EDGE,"E37.9.1"),sQuery(id+"F12.wireOp",EDGE,"E37.10.0")])]}),makeQuery(id+"F13.opLoft","SWEPT_EDGE",EDGE,{"disambiguationData":[OSD([subQ0,sQuery(id+"F6.wireOp",EDGE,"E3.1"),sQuery(id+"F6.wireOp",EDGE,"E17.trimOffspring"),sQuery(id+"F7.wireOp",EDGE,"E20.9.0"),sQuery(id+"F7.wireOp",EDGE,"E20.9.1"),sQuery(id+"F8.wireOp",EDGE,"E24.8.3"),sQuery(id+"F8.wireOp",EDGE,"E24.9.2"),sQuery(id+"F9.wireOp",EDGE,"E27.8.0"),sQuery(id+"F9.wireOp",EDGE,"E27.8.1"),sQuery(id+"F10.wireOp",EDGE,"E31.8.1"),sQuery(id+"F10.wireOp",EDGE,"E31.9.0"),sQuery(id+"F11.wireOp",EDGE,"E34.9.0"),sQuery(id+"F11.wireOp",EDGE,"E34.9.1"),sQuery(id+"F12.wireOp",EDGE,"E37.8.1"),sQuery(id+"F12.wireOp",EDGE,"E37.9.0")])]})]);}
            var Q9;
            {Q9=qUnion([makeQuery(id+"F13.opLoft","SWEPT_EDGE",EDGE,{"disambiguationData":[OSD([sQuery(id+"F6.wireOp",EDGE,"E1.0"),sQuery(id+"F6.wireOp",EDGE,"E17.trimOffspring"),sQuery(id+"F7.wireOp",EDGE,"E20.9.0"),sQuery(id+"F7.wireOp",EDGE,"E20.10.1"),sQuery(id+"F8.wireOp",EDGE,"E24.9.2"),sQuery(id+"F8.wireOp",EDGE,"E24.9.3"),sQuery(id+"F9.wireOp",EDGE,"E27.8.1"),sQuery(id+"F9.wireOp",EDGE,"E27.9.0"),sQuery(id+"F10.wireOp",EDGE,"E31.9.0"),sQuery(id+"F10.wireOp",EDGE,"E31.9.1"),sQuery(id+"F11.wireOp",EDGE,"E34.9.1"),sQuery(id+"F11.wireOp",EDGE,"E34.10.0"),sQuery(id+"F12.wireOp",EDGE,"E37.9.0"),sQuery(id+"F12.wireOp",EDGE,"E37.9.1")])]}),makeQuery(id+"F13.opLoft","SWEPT_EDGE",EDGE,{"disambiguationData":[OSD([sQuery(id+"F6.wireOp",EDGE,"E5.0"),sQuery(id+"F6.wireOp",EDGE,"E6.trimOffspring"),sQuery(id+"F7.wireOp",EDGE,"E20.10.0"),sQuery(id+"F7.wireOp",EDGE,"E20.11.1"),sQuery(id+"F8.wireOp",EDGE,"E24.10.2"),sQuery(id+"F8.wireOp",EDGE,"E24.10.3"),sQuery(id+"F9.wireOp",EDGE,"E27.9.1"),sQuery(id+"F9.wireOp",EDGE,"E27.10.0"),sQuery(id+"F10.wireOp",EDGE,"E31.10.0"),sQuery(id+"F10.wireOp",EDGE,"E31.10.1"),sQuery(id+"F11.wireOp",EDGE,"E34.10.1"),sQuery(id+"F11.wireOp",EDGE,"E34.11.0"),sQuery(id+"F12.wireOp",EDGE,"E37.10.0"),sQuery(id+"F12.wireOp",EDGE,"E37.10.1")])]})]);}
            var Q10;
            {var subQ0=sQuery(id+"F6.wireOp",EDGE,"E0");Q10=qUnion([makeQuery(id+"F13.opLoft","SWEPT_EDGE",EDGE,{"disambiguationData":[OSD([subQ0,sQuery(id+"F6.wireOp",EDGE,"E1.0"),sQuery(id+"F6.wireOp",EDGE,"E6.trimOffspring"),sQuery(id+"F7.wireOp",EDGE,"E20.10.0"),sQuery(id+"F7.wireOp",EDGE,"E20.10.1"),sQuery(id+"F8.wireOp",EDGE,"E24.9.3"),sQuery(id+"F8.wireOp",EDGE,"E24.10.2"),sQuery(id+"F9.wireOp",EDGE,"E27.9.0"),sQuery(id+"F9.wireOp",EDGE,"E27.9.1"),sQuery(id+"F10.wireOp",EDGE,"E31.9.1"),sQuery(id+"F10.wireOp",EDGE,"E31.10.0"),sQuery(id+"F11.wireOp",EDGE,"E34.10.0"),sQuery(id+"F11.wireOp",EDGE,"E34.10.1"),sQuery(id+"F12.wireOp",EDGE,"E37.9.1"),sQuery(id+"F12.wireOp",EDGE,"E37.10.0")])]}),makeQuery(id+"F13.opLoft","SWEPT_EDGE",EDGE,{"disambiguationData":[OSD([subQ0,sQuery(id+"F6.wireOp",EDGE,"E5.0"),sQuery(id+"F6.wireOp",EDGE,"E8.trimOffspring"),sQuery(id+"F7.wireOp",EDGE,"E20.11.0"),sQuery(id+"F7.wireOp",EDGE,"E20.11.1"),sQuery(id+"F8.wireOp",EDGE,"E24.10.3"),sQuery(id+"F8.wireOp",EDGE,"E24.11.2"),sQuery(id+"F9.wireOp",EDGE,"E27.10.0"),sQuery(id+"F9.wireOp",EDGE,"E27.10.1"),sQuery(id+"F10.wireOp",EDGE,"E31.10.1"),sQuery(id+"F10.wireOp",EDGE,"E31.11.0"),sQuery(id+"F11.wireOp",EDGE,"E34.11.0"),sQuery(id+"F11.wireOp",EDGE,"E34.11.1"),sQuery(id+"F12.wireOp",EDGE,"E37.10.1"),sQuery(id+"F12.wireOp",EDGE,"E37.11.0")])]})]);}
            var Q11;
            {var subQ0=sQuery(id+"F6.wireOp",EDGE,"E0");Q11=qUnion([makeQuery(id+"F13.opLoft","SWEPT_EDGE",EDGE,{"disambiguationData":[OSD([subQ0,sQuery(id+"F6.wireOp",EDGE,"E4.0"),sQuery(id+"F6.wireOp",EDGE,"E9.trimOffspring"),sQuery(id+"F7.wireOp",EDGE,"E18"),sQuery(id+"F7.wireOp",EDGE,"E19"),sQuery(id+"F8.wireOp",EDGE,"E23"),sQuery(id+"F8.wireOp",EDGE,"E24.11.3"),sQuery(id+"F9.wireOp",EDGE,"E27.11.0"),sQuery(id+"F9.wireOp",EDGE,"E27.11.1"),sQuery(id+"F10.wireOp",EDGE,"E30"),sQuery(id+"F10.wireOp",EDGE,"E31.11.1"),sQuery(id+"F11.wireOp",EDGE,"E32"),sQuery(id+"F11.wireOp",EDGE,"E33"),sQuery(id+"F12.wireOp",EDGE,"E36"),sQuery(id+"F12.wireOp",EDGE,"E37.11.1")])]}),makeQuery(id+"F13.opLoft","SWEPT_EDGE",EDGE,{"disambiguationData":[OSD([subQ0,sQuery(id+"F6.wireOp",EDGE,"E5.0"),sQuery(id+"F6.wireOp",EDGE,"E8.trimOffspring"),sQuery(id+"F7.wireOp",EDGE,"E20.11.0"),sQuery(id+"F7.wireOp",EDGE,"E20.11.1"),sQuery(id+"F8.wireOp",EDGE,"E24.10.3"),sQuery(id+"F8.wireOp",EDGE,"E24.11.2"),sQuery(id+"F9.wireOp",EDGE,"E27.10.0"),sQuery(id+"F9.wireOp",EDGE,"E27.10.1"),sQuery(id+"F10.wireOp",EDGE,"E31.10.1"),sQuery(id+"F10.wireOp",EDGE,"E31.11.0"),sQuery(id+"F11.wireOp",EDGE,"E34.11.0"),sQuery(id+"F11.wireOp",EDGE,"E34.11.1"),sQuery(id+"F12.wireOp",EDGE,"E37.10.1"),sQuery(id+"F12.wireOp",EDGE,"E37.11.0")])]})]);}
            var Q12;
            {Q12=qUnion([makeQuery(id+"F13.opLoft","SWEPT_EDGE",EDGE,{"disambiguationData":[OSD([sQuery(id+"F6.wireOp",EDGE,"E3.0"),sQuery(id+"F6.wireOp",EDGE,"E9.trimOffspring"),sQuery(id+"F7.wireOp",EDGE,"E18"),sQuery(id+"F7.wireOp",EDGE,"E20.1.1"),sQuery(id+"F8.wireOp",EDGE,"E22"),sQuery(id+"F8.wireOp",EDGE,"E23"),sQuery(id+"F9.wireOp",EDGE,"E26"),sQuery(id+"F9.wireOp",EDGE,"E27.11.1"),sQuery(id+"F10.wireOp",EDGE,"E29"),sQuery(id+"F10.wireOp",EDGE,"E30"),sQuery(id+"F11.wireOp",EDGE,"E32"),sQuery(id+"F11.wireOp",EDGE,"E34.1.0"),sQuery(id+"F12.wireOp",EDGE,"E35"),sQuery(id+"F12.wireOp",EDGE,"E36")])]}),makeQuery(id+"F13.opLoft","SWEPT_EDGE",EDGE,{"disambiguationData":[OSD([sQuery(id+"F6.wireOp",EDGE,"E4.0"),sQuery(id+"F6.wireOp",EDGE,"E8.trimOffspring"),sQuery(id+"F7.wireOp",EDGE,"E19"),sQuery(id+"F7.wireOp",EDGE,"E20.11.0"),sQuery(id+"F8.wireOp",EDGE,"E24.11.2"),sQuery(id+"F8.wireOp",EDGE,"E24.11.3"),sQuery(id+"F9.wireOp",EDGE,"E27.10.1"),sQuery(id+"F9.wireOp",EDGE,"E27.11.0"),sQuery(id+"F10.wireOp",EDGE,"E31.11.0"),sQuery(id+"F10.wireOp",EDGE,"E31.11.1"),sQuery(id+"F11.wireOp",EDGE,"E33"),sQuery(id+"F11.wireOp",EDGE,"E34.11.1"),sQuery(id+"F12.wireOp",EDGE,"E37.11.0"),sQuery(id+"F12.wireOp",EDGE,"E37.11.1")])]})]);}
            var Q13;
            {var subQ0=sQuery(id+"F6.wireOp",EDGE,"E0");Q13=qUnion([makeQuery(id+"F13.opLoft","SWEPT_EDGE",EDGE,{"disambiguationData":[OSD([subQ0,sQuery(id+"F6.wireOp",EDGE,"E3.0"),sQuery(id+"F6.wireOp",EDGE,"E10.trimOffspring"),sQuery(id+"F7.wireOp",EDGE,"E20.1.0"),sQuery(id+"F7.wireOp",EDGE,"E20.1.1"),sQuery(id+"F8.wireOp",EDGE,"E22"),sQuery(id+"F8.wireOp",EDGE,"E24.1.2"),sQuery(id+"F9.wireOp",EDGE,"E25"),sQuery(id+"F9.wireOp",EDGE,"E26"),sQuery(id+"F10.wireOp",EDGE,"E29"),sQuery(id+"F10.wireOp",EDGE,"E31.1.0"),sQuery(id+"F11.wireOp",EDGE,"E34.1.0"),sQuery(id+"F11.wireOp",EDGE,"E34.1.1"),sQuery(id+"F12.wireOp",EDGE,"E35"),sQuery(id+"F12.wireOp",EDGE,"E37.1.0")])]}),makeQuery(id+"F13.opLoft","SWEPT_EDGE",EDGE,{"disambiguationData":[OSD([subQ0,sQuery(id+"F6.wireOp",EDGE,"E4.0"),sQuery(id+"F6.wireOp",EDGE,"E9.trimOffspring"),sQuery(id+"F7.wireOp",EDGE,"E18"),sQuery(id+"F7.wireOp",EDGE,"E19"),sQuery(id+"F8.wireOp",EDGE,"E23"),sQuery(id+"F8.wireOp",EDGE,"E24.11.3"),sQuery(id+"F9.wireOp",EDGE,"E27.11.0"),sQuery(id+"F9.wireOp",EDGE,"E27.11.1"),sQuery(id+"F10.wireOp",EDGE,"E30"),sQuery(id+"F10.wireOp",EDGE,"E31.11.1"),sQuery(id+"F11.wireOp",EDGE,"E32"),sQuery(id+"F11.wireOp",EDGE,"E33"),sQuery(id+"F12.wireOp",EDGE,"E36"),sQuery(id+"F12.wireOp",EDGE,"E37.11.1")])]})]);}
            var Q14;
            {var subQ0=sQuery(id+"F6.wireOp",EDGE,"E0");Q14=qUnion([makeQuery(id+"F13.opLoft","SWEPT_EDGE",EDGE,{"disambiguationData":[OSD([subQ0,sQuery(id+"F6.wireOp",EDGE,"E1.2"),sQuery(id+"F6.wireOp",EDGE,"E11.trimOffspring"),sQuery(id+"F7.wireOp",EDGE,"E20.2.0"),sQuery(id+"F7.wireOp",EDGE,"E20.2.1"),sQuery(id+"F8.wireOp",EDGE,"E24.1.3"),sQuery(id+"F8.wireOp",EDGE,"E24.2.2"),sQuery(id+"F9.wireOp",EDGE,"E27.1.0"),sQuery(id+"F9.wireOp",EDGE,"E27.1.1"),sQuery(id+"F10.wireOp",EDGE,"E31.1.1"),sQuery(id+"F10.wireOp",EDGE,"E31.2.0"),sQuery(id+"F11.wireOp",EDGE,"E34.2.0"),sQuery(id+"F11.wireOp",EDGE,"E34.2.1"),sQuery(id+"F12.wireOp",EDGE,"E37.1.1"),sQuery(id+"F12.wireOp",EDGE,"E37.2.0")])]}),makeQuery(id+"F13.opLoft","SWEPT_EDGE",EDGE,{"disambiguationData":[OSD([subQ0,sQuery(id+"F6.wireOp",EDGE,"E3.0"),sQuery(id+"F6.wireOp",EDGE,"E10.trimOffspring"),sQuery(id+"F7.wireOp",EDGE,"E20.1.0"),sQuery(id+"F7.wireOp",EDGE,"E20.1.1"),sQuery(id+"F8.wireOp",EDGE,"E22"),sQuery(id+"F8.wireOp",EDGE,"E24.1.2"),sQuery(id+"F9.wireOp",EDGE,"E25"),sQuery(id+"F9.wireOp",EDGE,"E26"),sQuery(id+"F10.wireOp",EDGE,"E29"),sQuery(id+"F10.wireOp",EDGE,"E31.1.0"),sQuery(id+"F11.wireOp",EDGE,"E34.1.0"),sQuery(id+"F11.wireOp",EDGE,"E34.1.1"),sQuery(id+"F12.wireOp",EDGE,"E35"),sQuery(id+"F12.wireOp",EDGE,"E37.1.0")])]})]);}
            var Q15;
            {Q15=qUnion([makeQuery(id+"F13.opLoft","SWEPT_EDGE",EDGE,{"disambiguationData":[OSD([sQuery(id+"F6.wireOp",EDGE,"E1.2"),sQuery(id+"F6.wireOp",EDGE,"E10.trimOffspring"),sQuery(id+"F7.wireOp",EDGE,"E20.1.0"),sQuery(id+"F7.wireOp",EDGE,"E20.2.1"),sQuery(id+"F8.wireOp",EDGE,"E24.1.2"),sQuery(id+"F8.wireOp",EDGE,"E24.1.3"),sQuery(id+"F9.wireOp",EDGE,"E25"),sQuery(id+"F9.wireOp",EDGE,"E27.1.0"),sQuery(id+"F10.wireOp",EDGE,"E31.1.0"),sQuery(id+"F10.wireOp",EDGE,"E31.1.1"),sQuery(id+"F11.wireOp",EDGE,"E34.1.1"),sQuery(id+"F11.wireOp",EDGE,"E34.2.0"),sQuery(id+"F12.wireOp",EDGE,"E37.1.0"),sQuery(id+"F12.wireOp",EDGE,"E37.1.1")])]}),makeQuery(id+"F13.opLoft","SWEPT_EDGE",EDGE,{"disambiguationData":[OSD([sQuery(id+"F6.wireOp",EDGE,"E3.0"),sQuery(id+"F6.wireOp",EDGE,"E9.trimOffspring"),sQuery(id+"F7.wireOp",EDGE,"E18"),sQuery(id+"F7.wireOp",EDGE,"E20.1.1"),sQuery(id+"F8.wireOp",EDGE,"E22"),sQuery(id+"F8.wireOp",EDGE,"E23"),sQuery(id+"F9.wireOp",EDGE,"E26"),sQuery(id+"F9.wireOp",EDGE,"E27.11.1"),sQuery(id+"F10.wireOp",EDGE,"E29"),sQuery(id+"F10.wireOp",EDGE,"E30"),sQuery(id+"F11.wireOp",EDGE,"E32"),sQuery(id+"F11.wireOp",EDGE,"E34.1.0"),sQuery(id+"F12.wireOp",EDGE,"E35"),sQuery(id+"F12.wireOp",EDGE,"E36")])]})]);}
            var Q16;
            {Q16=qUnion([makeQuery(id+"F13.opLoft","SWEPT_EDGE",EDGE,{"disambiguationData":[OSD([sQuery(id+"F6.wireOp",EDGE,"E1.2"),sQuery(id+"F6.wireOp",EDGE,"E10.trimOffspring"),sQuery(id+"F7.wireOp",EDGE,"E20.1.0"),sQuery(id+"F7.wireOp",EDGE,"E20.2.1"),sQuery(id+"F8.wireOp",EDGE,"E24.1.2"),sQuery(id+"F8.wireOp",EDGE,"E24.1.3"),sQuery(id+"F9.wireOp",EDGE,"E25"),sQuery(id+"F9.wireOp",EDGE,"E27.1.0"),sQuery(id+"F10.wireOp",EDGE,"E31.1.0"),sQuery(id+"F10.wireOp",EDGE,"E31.1.1"),sQuery(id+"F11.wireOp",EDGE,"E34.1.1"),sQuery(id+"F11.wireOp",EDGE,"E34.2.0"),sQuery(id+"F12.wireOp",EDGE,"E37.1.0"),sQuery(id+"F12.wireOp",EDGE,"E37.1.1")])]}),makeQuery(id+"F13.opLoft","SWEPT_EDGE",EDGE,{"disambiguationData":[OSD([sQuery(id+"F6.wireOp",EDGE,"E5.2"),sQuery(id+"F6.wireOp",EDGE,"E11.trimOffspring"),sQuery(id+"F7.wireOp",EDGE,"E20.2.0"),sQuery(id+"F7.wireOp",EDGE,"E20.3.1"),sQuery(id+"F8.wireOp",EDGE,"E24.2.2"),sQuery(id+"F8.wireOp",EDGE,"E24.2.3"),sQuery(id+"F9.wireOp",EDGE,"E27.1.1"),sQuery(id+"F9.wireOp",EDGE,"E27.2.0"),sQuery(id+"F10.wireOp",EDGE,"E31.2.0"),sQuery(id+"F10.wireOp",EDGE,"E31.2.1"),sQuery(id+"F11.wireOp",EDGE,"E34.2.1"),sQuery(id+"F11.wireOp",EDGE,"E34.3.0"),sQuery(id+"F12.wireOp",EDGE,"E37.2.0"),sQuery(id+"F12.wireOp",EDGE,"E37.2.1")])]})]);}
            var Q17;
            {var subQ0=sQuery(id+"F6.wireOp",EDGE,"E0");Q17=qUnion([makeQuery(id+"F13.opLoft","SWEPT_EDGE",EDGE,{"disambiguationData":[OSD([subQ0,sQuery(id+"F6.wireOp",EDGE,"E1.2"),sQuery(id+"F6.wireOp",EDGE,"E11.trimOffspring"),sQuery(id+"F7.wireOp",EDGE,"E20.2.0"),sQuery(id+"F7.wireOp",EDGE,"E20.2.1"),sQuery(id+"F8.wireOp",EDGE,"E24.1.3"),sQuery(id+"F8.wireOp",EDGE,"E24.2.2"),sQuery(id+"F9.wireOp",EDGE,"E27.1.0"),sQuery(id+"F9.wireOp",EDGE,"E27.1.1"),sQuery(id+"F10.wireOp",EDGE,"E31.1.1"),sQuery(id+"F10.wireOp",EDGE,"E31.2.0"),sQuery(id+"F11.wireOp",EDGE,"E34.2.0"),sQuery(id+"F11.wireOp",EDGE,"E34.2.1"),sQuery(id+"F12.wireOp",EDGE,"E37.1.1"),sQuery(id+"F12.wireOp",EDGE,"E37.2.0")])]}),makeQuery(id+"F13.opLoft","SWEPT_EDGE",EDGE,{"disambiguationData":[OSD([subQ0,sQuery(id+"F6.wireOp",EDGE,"E5.2"),sQuery(id+"F6.wireOp",EDGE,"E12.trimOffspring"),sQuery(id+"F7.wireOp",EDGE,"E20.3.0"),sQuery(id+"F7.wireOp",EDGE,"E20.3.1"),sQuery(id+"F8.wireOp",EDGE,"E24.2.3"),sQuery(id+"F8.wireOp",EDGE,"E24.3.2"),sQuery(id+"F9.wireOp",EDGE,"E27.2.0"),sQuery(id+"F9.wireOp",EDGE,"E27.2.1"),sQuery(id+"F10.wireOp",EDGE,"E31.2.1"),sQuery(id+"F10.wireOp",EDGE,"E31.3.0"),sQuery(id+"F11.wireOp",EDGE,"E34.3.0"),sQuery(id+"F11.wireOp",EDGE,"E34.3.1"),sQuery(id+"F12.wireOp",EDGE,"E37.2.1"),sQuery(id+"F12.wireOp",EDGE,"E37.3.0")])]})]);}
            var Q18;
            {Q18=qUnion([makeQuery(id+"F13.opLoft","SWEPT_EDGE",EDGE,{"disambiguationData":[OSD([sQuery(id+"F6.wireOp",EDGE,"E4.2"),sQuery(id+"F6.wireOp",EDGE,"E12.trimOffspring"),sQuery(id+"F7.wireOp",EDGE,"E20.3.0"),sQuery(id+"F7.wireOp",EDGE,"E20.4.1"),sQuery(id+"F8.wireOp",EDGE,"E24.3.2"),sQuery(id+"F8.wireOp",EDGE,"E24.3.3"),sQuery(id+"F9.wireOp",EDGE,"E27.2.1"),sQuery(id+"F9.wireOp",EDGE,"E27.3.0"),sQuery(id+"F10.wireOp",EDGE,"E31.3.0"),sQuery(id+"F10.wireOp",EDGE,"E31.3.1"),sQuery(id+"F11.wireOp",EDGE,"E34.3.1"),sQuery(id+"F11.wireOp",EDGE,"E34.4.0"),sQuery(id+"F12.wireOp",EDGE,"E37.3.0"),sQuery(id+"F12.wireOp",EDGE,"E37.3.1")])]}),makeQuery(id+"F13.opLoft","SWEPT_EDGE",EDGE,{"disambiguationData":[OSD([sQuery(id+"F6.wireOp",EDGE,"E5.2"),sQuery(id+"F6.wireOp",EDGE,"E11.trimOffspring"),sQuery(id+"F7.wireOp",EDGE,"E20.2.0"),sQuery(id+"F7.wireOp",EDGE,"E20.3.1"),sQuery(id+"F8.wireOp",EDGE,"E24.2.2"),sQuery(id+"F8.wireOp",EDGE,"E24.2.3"),sQuery(id+"F9.wireOp",EDGE,"E27.1.1"),sQuery(id+"F9.wireOp",EDGE,"E27.2.0"),sQuery(id+"F10.wireOp",EDGE,"E31.2.0"),sQuery(id+"F10.wireOp",EDGE,"E31.2.1"),sQuery(id+"F11.wireOp",EDGE,"E34.2.1"),sQuery(id+"F11.wireOp",EDGE,"E34.3.0"),sQuery(id+"F12.wireOp",EDGE,"E37.2.0"),sQuery(id+"F12.wireOp",EDGE,"E37.2.1")])]})]);}
            var Q19;
            {var subQ0=sQuery(id+"F6.wireOp",EDGE,"E0");Q19=qUnion([makeQuery(id+"F13.opLoft","SWEPT_EDGE",EDGE,{"disambiguationData":[OSD([subQ0,sQuery(id+"F6.wireOp",EDGE,"E4.2"),sQuery(id+"F6.wireOp",EDGE,"E13.trimOffspring"),sQuery(id+"F7.wireOp",EDGE,"E20.4.0"),sQuery(id+"F7.wireOp",EDGE,"E20.4.1"),sQuery(id+"F8.wireOp",EDGE,"E24.3.3"),sQuery(id+"F8.wireOp",EDGE,"E24.4.2"),sQuery(id+"F9.wireOp",EDGE,"E27.3.0"),sQuery(id+"F9.wireOp",EDGE,"E27.3.1"),sQuery(id+"F10.wireOp",EDGE,"E31.3.1"),sQuery(id+"F10.wireOp",EDGE,"E31.4.0"),sQuery(id+"F11.wireOp",EDGE,"E34.4.0"),sQuery(id+"F11.wireOp",EDGE,"E34.4.1"),sQuery(id+"F12.wireOp",EDGE,"E37.3.1"),sQuery(id+"F12.wireOp",EDGE,"E37.4.0")])]}),makeQuery(id+"F13.opLoft","SWEPT_EDGE",EDGE,{"disambiguationData":[OSD([subQ0,sQuery(id+"F6.wireOp",EDGE,"E5.2"),sQuery(id+"F6.wireOp",EDGE,"E12.trimOffspring"),sQuery(id+"F7.wireOp",EDGE,"E20.3.0"),sQuery(id+"F7.wireOp",EDGE,"E20.3.1"),sQuery(id+"F8.wireOp",EDGE,"E24.2.3"),sQuery(id+"F8.wireOp",EDGE,"E24.3.2"),sQuery(id+"F9.wireOp",EDGE,"E27.2.0"),sQuery(id+"F9.wireOp",EDGE,"E27.2.1"),sQuery(id+"F10.wireOp",EDGE,"E31.2.1"),sQuery(id+"F10.wireOp",EDGE,"E31.3.0"),sQuery(id+"F11.wireOp",EDGE,"E34.3.0"),sQuery(id+"F11.wireOp",EDGE,"E34.3.1"),sQuery(id+"F12.wireOp",EDGE,"E37.2.1"),sQuery(id+"F12.wireOp",EDGE,"E37.3.0")])]})]);}
            var Q20;
            {Q20=qUnion([makeQuery(id+"F13.opLoft","SWEPT_EDGE",EDGE,{"disambiguationData":[OSD([sQuery(id+"F6.wireOp",EDGE,"E3.2"),sQuery(id+"F6.wireOp",EDGE,"E13.trimOffspring"),sQuery(id+"F7.wireOp",EDGE,"E20.4.0"),sQuery(id+"F7.wireOp",EDGE,"E20.5.1"),sQuery(id+"F8.wireOp",EDGE,"E24.4.2"),sQuery(id+"F8.wireOp",EDGE,"E24.4.3"),sQuery(id+"F9.wireOp",EDGE,"E27.3.1"),sQuery(id+"F9.wireOp",EDGE,"E27.4.0"),sQuery(id+"F10.wireOp",EDGE,"E31.4.0"),sQuery(id+"F10.wireOp",EDGE,"E31.4.1"),sQuery(id+"F11.wireOp",EDGE,"E34.4.1"),sQuery(id+"F11.wireOp",EDGE,"E34.5.0"),sQuery(id+"F12.wireOp",EDGE,"E37.4.0"),sQuery(id+"F12.wireOp",EDGE,"E37.4.1")])]}),makeQuery(id+"F13.opLoft","SWEPT_EDGE",EDGE,{"disambiguationData":[OSD([sQuery(id+"F6.wireOp",EDGE,"E4.2"),sQuery(id+"F6.wireOp",EDGE,"E12.trimOffspring"),sQuery(id+"F7.wireOp",EDGE,"E20.3.0"),sQuery(id+"F7.wireOp",EDGE,"E20.4.1"),sQuery(id+"F8.wireOp",EDGE,"E24.3.2"),sQuery(id+"F8.wireOp",EDGE,"E24.3.3"),sQuery(id+"F9.wireOp",EDGE,"E27.2.1"),sQuery(id+"F9.wireOp",EDGE,"E27.3.0"),sQuery(id+"F10.wireOp",EDGE,"E31.3.0"),sQuery(id+"F10.wireOp",EDGE,"E31.3.1"),sQuery(id+"F11.wireOp",EDGE,"E34.3.1"),sQuery(id+"F11.wireOp",EDGE,"E34.4.0"),sQuery(id+"F12.wireOp",EDGE,"E37.3.0"),sQuery(id+"F12.wireOp",EDGE,"E37.3.1")])]})]);}
            var Q21;
            {var subQ0=sQuery(id+"F6.wireOp",EDGE,"E0");Q21=qUnion([makeQuery(id+"F13.opLoft","SWEPT_EDGE",EDGE,{"disambiguationData":[OSD([subQ0,sQuery(id+"F6.wireOp",EDGE,"E3.2"),sQuery(id+"F6.wireOp",EDGE,"E14.trimOffspring"),sQuery(id+"F7.wireOp",EDGE,"E20.5.0"),sQuery(id+"F7.wireOp",EDGE,"E20.5.1"),sQuery(id+"F8.wireOp",EDGE,"E24.4.3"),sQuery(id+"F8.wireOp",EDGE,"E24.5.2"),sQuery(id+"F9.wireOp",EDGE,"E27.4.0"),sQuery(id+"F9.wireOp",EDGE,"E27.4.1"),sQuery(id+"F10.wireOp",EDGE,"E31.4.1"),sQuery(id+"F10.wireOp",EDGE,"E31.5.0"),sQuery(id+"F11.wireOp",EDGE,"E34.5.0"),sQuery(id+"F11.wireOp",EDGE,"E34.5.1"),sQuery(id+"F12.wireOp",EDGE,"E37.4.1"),sQuery(id+"F12.wireOp",EDGE,"E37.5.0")])]}),makeQuery(id+"F13.opLoft","SWEPT_EDGE",EDGE,{"disambiguationData":[OSD([subQ0,sQuery(id+"F6.wireOp",EDGE,"E4.2"),sQuery(id+"F6.wireOp",EDGE,"E13.trimOffspring"),sQuery(id+"F7.wireOp",EDGE,"E20.4.0"),sQuery(id+"F7.wireOp",EDGE,"E20.4.1"),sQuery(id+"F8.wireOp",EDGE,"E24.3.3"),sQuery(id+"F8.wireOp",EDGE,"E24.4.2"),sQuery(id+"F9.wireOp",EDGE,"E27.3.0"),sQuery(id+"F9.wireOp",EDGE,"E27.3.1"),sQuery(id+"F10.wireOp",EDGE,"E31.3.1"),sQuery(id+"F10.wireOp",EDGE,"E31.4.0"),sQuery(id+"F11.wireOp",EDGE,"E34.4.0"),sQuery(id+"F11.wireOp",EDGE,"E34.4.1"),sQuery(id+"F12.wireOp",EDGE,"E37.3.1"),sQuery(id+"F12.wireOp",EDGE,"E37.4.0")])]})]);}
            var Q22;
            {Q22=qUnion([makeQuery(id+"F13.opLoft","SWEPT_EDGE",EDGE,{"disambiguationData":[OSD([sQuery(id+"F6.wireOp",EDGE,"E1.1"),sQuery(id+"F6.wireOp",EDGE,"E14.trimOffspring"),sQuery(id+"F7.wireOp",EDGE,"E20.5.0"),sQuery(id+"F7.wireOp",EDGE,"E20.6.1"),sQuery(id+"F8.wireOp",EDGE,"E24.5.2"),sQuery(id+"F8.wireOp",EDGE,"E24.5.3"),sQuery(id+"F9.wireOp",EDGE,"E27.4.1"),sQuery(id+"F9.wireOp",EDGE,"E27.5.0"),sQuery(id+"F10.wireOp",EDGE,"E31.5.0"),sQuery(id+"F10.wireOp",EDGE,"E31.5.1"),sQuery(id+"F11.wireOp",EDGE,"E34.5.1"),sQuery(id+"F11.wireOp",EDGE,"E34.6.0"),sQuery(id+"F12.wireOp",EDGE,"E37.5.0"),sQuery(id+"F12.wireOp",EDGE,"E37.5.1")])]}),makeQuery(id+"F13.opLoft","SWEPT_EDGE",EDGE,{"disambiguationData":[OSD([sQuery(id+"F6.wireOp",EDGE,"E3.2"),sQuery(id+"F6.wireOp",EDGE,"E13.trimOffspring"),sQuery(id+"F7.wireOp",EDGE,"E20.4.0"),sQuery(id+"F7.wireOp",EDGE,"E20.5.1"),sQuery(id+"F8.wireOp",EDGE,"E24.4.2"),sQuery(id+"F8.wireOp",EDGE,"E24.4.3"),sQuery(id+"F9.wireOp",EDGE,"E27.3.1"),sQuery(id+"F9.wireOp",EDGE,"E27.4.0"),sQuery(id+"F10.wireOp",EDGE,"E31.4.0"),sQuery(id+"F10.wireOp",EDGE,"E31.4.1"),sQuery(id+"F11.wireOp",EDGE,"E34.4.1"),sQuery(id+"F11.wireOp",EDGE,"E34.5.0"),sQuery(id+"F12.wireOp",EDGE,"E37.4.0"),sQuery(id+"F12.wireOp",EDGE,"E37.4.1")])]})]);}
            var Q23;
            {var subQ0=sQuery(id+"F6.wireOp",EDGE,"E0");Q23=qUnion([makeQuery(id+"F13.opLoft","SWEPT_EDGE",EDGE,{"disambiguationData":[OSD([subQ0,sQuery(id+"F6.wireOp",EDGE,"E1.1"),sQuery(id+"F6.wireOp",EDGE,"E15.trimOffspring"),sQuery(id+"F7.wireOp",EDGE,"E20.6.0"),sQuery(id+"F7.wireOp",EDGE,"E20.6.1"),sQuery(id+"F8.wireOp",EDGE,"E24.5.3"),sQuery(id+"F8.wireOp",EDGE,"E24.6.2"),sQuery(id+"F9.wireOp",EDGE,"E27.5.0"),sQuery(id+"F9.wireOp",EDGE,"E27.5.1"),sQuery(id+"F10.wireOp",EDGE,"E31.5.1"),sQuery(id+"F10.wireOp",EDGE,"E31.6.0"),sQuery(id+"F11.wireOp",EDGE,"E34.6.0"),sQuery(id+"F11.wireOp",EDGE,"E34.6.1"),sQuery(id+"F12.wireOp",EDGE,"E37.5.1"),sQuery(id+"F12.wireOp",EDGE,"E37.6.0")])]}),makeQuery(id+"F13.opLoft","SWEPT_EDGE",EDGE,{"disambiguationData":[OSD([subQ0,sQuery(id+"F6.wireOp",EDGE,"E3.2"),sQuery(id+"F6.wireOp",EDGE,"E14.trimOffspring"),sQuery(id+"F7.wireOp",EDGE,"E20.5.0"),sQuery(id+"F7.wireOp",EDGE,"E20.5.1"),sQuery(id+"F8.wireOp",EDGE,"E24.4.3"),sQuery(id+"F8.wireOp",EDGE,"E24.5.2"),sQuery(id+"F9.wireOp",EDGE,"E27.4.0"),sQuery(id+"F9.wireOp",EDGE,"E27.4.1"),sQuery(id+"F10.wireOp",EDGE,"E31.4.1"),sQuery(id+"F10.wireOp",EDGE,"E31.5.0"),sQuery(id+"F11.wireOp",EDGE,"E34.5.0"),sQuery(id+"F11.wireOp",EDGE,"E34.5.1"),sQuery(id+"F12.wireOp",EDGE,"E37.4.1"),sQuery(id+"F12.wireOp",EDGE,"E37.5.0")])]})]);}
            fillet(context, id + "F14", {"entities" : qUnion([Q0, Q1, Q2, Q3, Q4, Q5, Q6, Q7, Q8, Q9, Q10, Q11, Q12, Q13, Q14, Q15, Q16, Q17, Q18, Q19, Q20, Q21, Q22, Q23]), "radius" : 1 * mm, "allowEdgeOverflow" : false});
        }
    });
